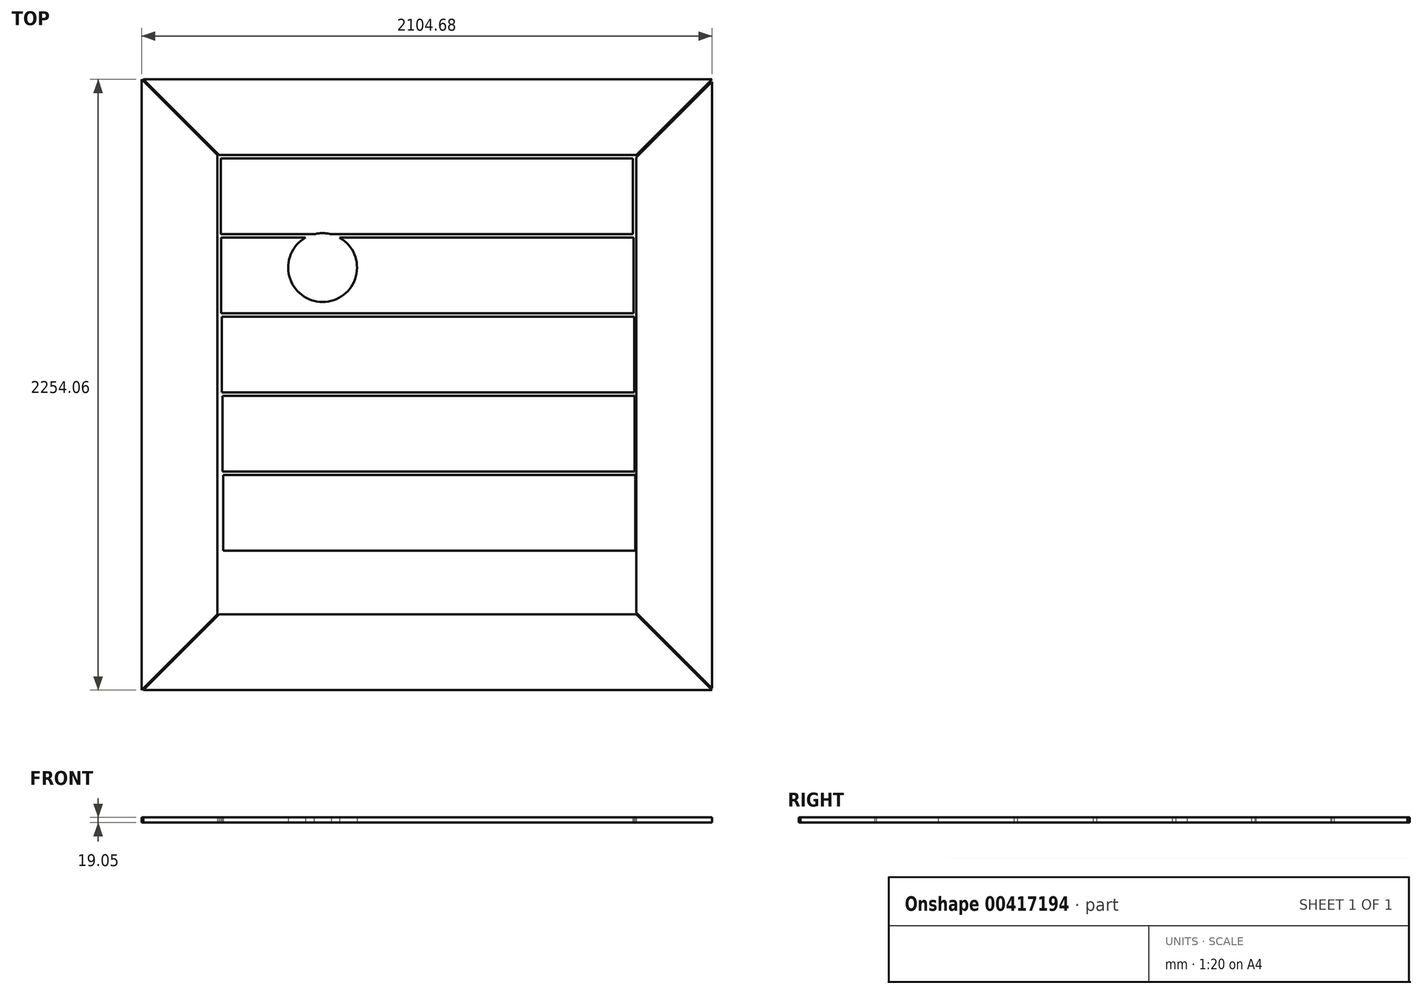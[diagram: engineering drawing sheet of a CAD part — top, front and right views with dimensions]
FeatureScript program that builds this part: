
annotation { "Feature Type Name" : "Feature", "Feature Type Description" : "" }
export const myFeature = defineFeature(function(context is Context, id is Id, definition is map)
    precondition{}
    {
        {
            var Q0;
            Q0=qCreatedBy(makeId("Top.planeOp"),FACE);
            var sketch = newSketch(context, id + "F0", { "sketchPlane" : qUnion([Q0])});
            skLineSegment(sketch, "E0", {"start": v(-1552.16, 176.72) * mm, "end": v(-1272.76, 456.12) * mm});
            skLineSegment(sketch, "E1", {"start": v(-1272.76, 456.12) * mm, "end": v(-1272.76, 2151.38) * mm});
            skLineSegment(sketch, "E2", {"start": v(-1272.76, 2151.38) * mm, "end": v(-1552.16, 2430.78) * mm});
            skLineSegment(sketch, "E3", {"start": v(-1552.16, 2430.78) * mm, "end": v(-1552.16, 176.72) * mm});
            skLineSegment(sketch, "E4", {"start": v(552.52, 176.72) * mm, "end": v(273.12, 456.12) * mm});
            skLineSegment(sketch, "E5", {"start": v(273.12, 456.12) * mm, "end": v(-1266.41, 456.12) * mm});
            skLineSegment(sketch, "E6", {"start": v(-1266.41, 456.12) * mm, "end": v(-1545.81, 176.72) * mm});
            skLineSegment(sketch, "E7", {"start": v(-1545.81, 176.72) * mm, "end": v(552.52, 176.72) * mm});
            skLineSegment(sketch, "E8", {"start": v(-1545.81, 2430.78) * mm, "end": v(-1266.41, 2151.38) * mm});
            skLineSegment(sketch, "E9", {"start": v(-1266.41, 2151.38) * mm, "end": v(273.12, 2151.38) * mm});
            skLineSegment(sketch, "E10", {"start": v(273.12, 2151.38) * mm, "end": v(552.52, 2430.78) * mm});
            skLineSegment(sketch, "E11", {"start": v(552.52, 2430.78) * mm, "end": v(-1545.81, 2430.78) * mm});
            skLineSegment(sketch, "E12", {"start": v(552.52, 2421.95) * mm, "end": v(273.12, 2142.55) * mm});
            skLineSegment(sketch, "E13", {"start": v(273.12, 2142.55) * mm, "end": v(273.12, 462.47) * mm});
            skLineSegment(sketch, "E14", {"start": v(273.12, 462.47) * mm, "end": v(552.52, 183.07) * mm});
            skLineSegment(sketch, "E15", {"start": v(552.52, 183.07) * mm, "end": v(552.52, 2421.95) * mm});
            skLineSegment(sketch, "E16.bottom", {"start": v(-1260.06, 2138.68) * mm, "end": v(260.42, 2138.68) * mm});
            skLineSegment(sketch, "E16.top", {"start": v(-1260.06, 1859.28) * mm, "end": v(260.42, 1859.28) * mm});
            skLineSegment(sketch, "E16.left", {"start": v(-1260.06, 2138.68) * mm, "end": v(-1260.06, 1859.28) * mm});
            skLineSegment(sketch, "E16.right", {"start": v(260.42, 2138.68) * mm, "end": v(260.42, 1859.28) * mm});
            skLineSegment(sketch, "E17.0.1.0", {"start": v(-1257.76, 1846.6) * mm, "end": v(262.73, 1846.6) * mm});
            skLineSegment(sketch, "E17.0.1.1", {"start": v(-1257.76, 1567.2) * mm, "end": v(262.73, 1567.2) * mm});
            skLineSegment(sketch, "E17.0.1.2", {"start": v(-1257.76, 1846.6) * mm, "end": v(-1257.76, 1567.2) * mm});
            skLineSegment(sketch, "E17.0.1.3", {"start": v(262.73, 1846.6) * mm, "end": v(262.73, 1567.2) * mm});
            skLineSegment(sketch, "E17.0.2.0", {"start": v(-1255.45, 1554.5) * mm, "end": v(265.03, 1554.5) * mm});
            skLineSegment(sketch, "E17.0.2.1", {"start": v(-1255.45, 1275.1) * mm, "end": v(265.03, 1275.1) * mm});
            skLineSegment(sketch, "E17.0.2.2", {"start": v(-1255.45, 1554.5) * mm, "end": v(-1255.45, 1275.1) * mm});
            skLineSegment(sketch, "E17.0.2.3", {"start": v(265.03, 1554.5) * mm, "end": v(265.03, 1275.1) * mm});
            skLineSegment(sketch, "E17.0.3.0", {"start": v(-1253.15, 1262.4) * mm, "end": v(267.34, 1262.4) * mm});
            skLineSegment(sketch, "E17.0.3.1", {"start": v(-1253.15, 983) * mm, "end": v(267.34, 983) * mm});
            skLineSegment(sketch, "E17.0.3.2", {"start": v(-1253.15, 1262.4) * mm, "end": v(-1253.15, 983) * mm});
            skLineSegment(sketch, "E17.0.3.3", {"start": v(267.34, 1262.4) * mm, "end": v(267.34, 983) * mm});
            skLineSegment(sketch, "E17.0.4.0", {"start": v(-1250.84, 970.32) * mm, "end": v(269.64, 970.32) * mm});
            skLineSegment(sketch, "E17.0.4.1", {"start": v(-1250.84, 690.92) * mm, "end": v(269.64, 690.92) * mm});
            skLineSegment(sketch, "E17.0.4.2", {"start": v(-1250.84, 970.32) * mm, "end": v(-1250.84, 690.92) * mm});
            skLineSegment(sketch, "E17.0.4.3", {"start": v(269.64, 970.32) * mm, "end": v(269.64, 690.92) * mm});
            skLineSegment(sketch, "E17.direction1", {"start": v(-1260.06, 1859.28) * mm, "end": v(-1234.66, 1859.28) * mm, "construction": true});
            skLineSegment(sketch, "E17.direction2", {"start": v(-1260.06, 1859.28) * mm, "end": v(-1257.76, 1567.2) * mm, "construction": true});
            skSolve(sketch);
        }
        {
            var Q0;
            Q0 = qSketchRegion(id + "F0", true);
            extrude(context, id + "F1", {"entities" : qUnion([Q0]), "depth" : 19.05 * mm});
        }
        {
            var Q0;
            Q0=qCreatedBy(makeId("Top.planeOp"),FACE);
            var sketch = newSketch(context, id + "F2", { "sketchPlane" : qUnion([Q0])});
            skCircle(sketch, "E18", {"center": v(-884.09, 1736.37) * mm, "radius": 127 * mm});
            skSolve(sketch);
        }
        {
            var Q0;
            Q0 = qSketchRegion(id + "F2", true);
            extrude(context, id + "F3", {"entities" : qUnion([Q0]), "operationType" : NewBodyOperationType.REMOVE, "endBound" : BoundingType.THROUGH_ALL, "depth" : 25.4 * mm, "hasSecondDirection" : true, "secondDirectionBound" : SecondDirectionBoundingType.THROUGH_ALL, "secondDirectionOppositeDirection" : true, "secondDirectionDepth" : 25.4 * mm});
        }
    });
